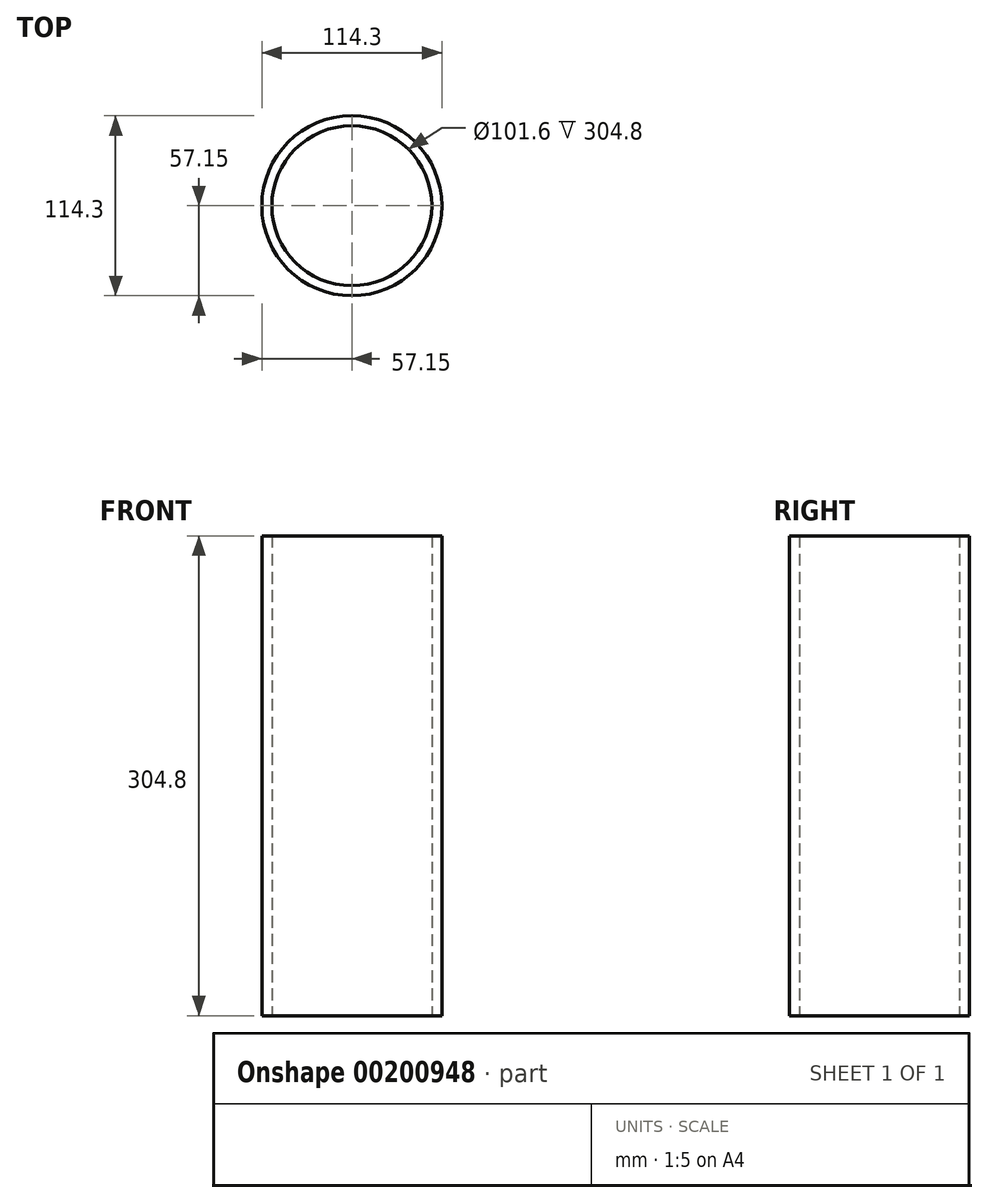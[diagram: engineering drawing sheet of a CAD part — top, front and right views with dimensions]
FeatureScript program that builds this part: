
annotation { "Feature Type Name" : "Feature", "Feature Type Description" : "" }
export const myFeature = defineFeature(function(context is Context, id is Id, definition is map)
    precondition{}
    {
        {
            var Q0;
            Q0=qCreatedBy(makeId("Top.planeOp"),FACE);
            var sketch = newSketch(context, id + "F0", { "sketchPlane" : qUnion([Q0])});
            skCircle(sketch, "E0", {"center": v(0, 0) * mm, "radius": 57.15 * mm});
            skCircle(sketch, "E1", {"center": v(0, 0) * mm, "radius": 50.8 * mm});
            skSolve(sketch);
        }
        {
            var Q0;
            Q0=makeQuery(id+"F0.imprint","IMPRINT",FACE,{"disambiguationData":[TD([[makeQuery(id+"F0.imprint","IMPRINT",EDGE,{"derivedFrom":sQuery(id+"F0.wireOp",EDGE,"E0")}),1.0]])]});
            extrude(context, id + "F1", {"entities" : qUnion([Q0]), "depth" : 304.8 * mm});
        }
    });
